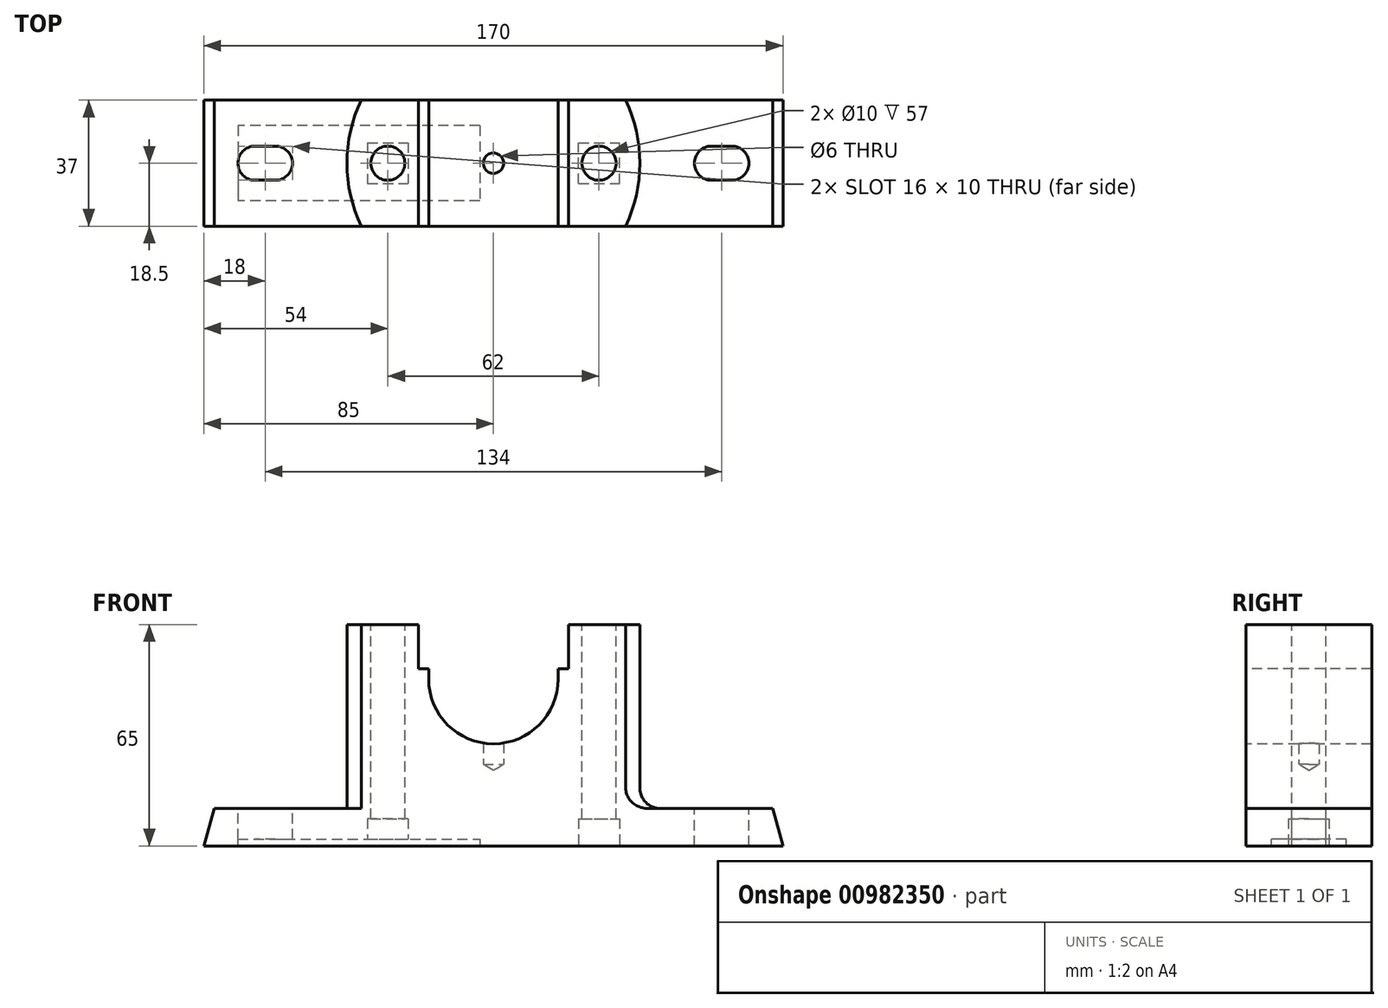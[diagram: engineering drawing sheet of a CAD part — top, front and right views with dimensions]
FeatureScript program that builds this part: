
annotation { "Feature Type Name" : "Feature", "Feature Type Description" : "" }
export const myFeature = defineFeature(function(context is Context, id is Id, definition is map)
    precondition{}
    {
        {
            var Q0;
            Q0=qCreatedBy(makeId("Front.planeOp"),FACE);
            var sketch = newSketch(context, id + "F0", { "sketchPlane" : qUnion([Q0])});
            skLineSegment(sketch, "E0", {"start": v(-85, 0) * mm, "end": v(85, 0) * mm});
            skLineSegment(sketch, "E1", {"start": v(-85, 0) * mm, "end": v(-82, 11) * mm});
            skLineSegment(sketch, "E2", {"start": v(0, 0) * mm, "end": v(0, 40.06) * mm, "construction": true});
            skLineSegment(sketch, "E3.MirrorCS", {"start": v(85, 0) * mm, "end": v(82, 11) * mm});
            skLineSegment(sketch, "E4", {"start": v(-82, 11) * mm, "end": v(82, 11) * mm});
            skSolve(sketch);
        }
        {
            var Q0;
            Q0=qSketchRegion(id+"F0",true);
            extrude(context, id + "F1", {"entities" : qUnion([Q0]), "endBound" : BoundingType.SYMMETRIC, "depth" : 37 * mm, "offsetDistance" : 25 * mm});
        }
        {
            var Q0;
            Q0=makeQuery(id+"F1.opExtrude","SWEPT_FACE",FACE,{"disambiguationData":[OSD([sQuery(id+"F0.wireOp",EDGE,"E4")])]});
            var sketch = newSketch(context, id + "F2", { "sketchPlane" : qUnion([Q0])});
            skArc(sketch, "E5", {"start": v(-38.82, 18.5) * mm, "mid": v(-43, 0) * mm, "end": v(-38.82, -18.5) * mm});
            skLineSegment(sketch, "E6.0", {"start": v(-38.82, 18.5) * mm, "end": v(38.82, 18.5) * mm});
            skLineSegment(sketch, "E6.1", {"start": v(-38.82, -18.5) * mm, "end": v(38.82, -18.5) * mm});
            skPoint(sketch, "E7.orphan", {"position": v(-82, 18.5) * mm});
            skPoint(sketch, "E8.orphan", {"position": v(82, 18.5) * mm});
            skPoint(sketch, "E9.orphan", {"position": v(82, -18.5) * mm});
            skArc(sketch, "E10.trimOffspring", {"start": v(38.82, -18.5) * mm, "mid": v(43, 0) * mm, "end": v(38.82, 18.5) * mm});
            skPoint(sketch, "E11.orphan", {"position": v(-82, -18.5) * mm});
            skSolve(sketch);
        }
        {
            var Q0;
            Q0=makeQuery(id+"F2.imprint","IMPRINT",FACE,{"disambiguationData":[TD([[makeQuery(id+"F2.imprint","IMPRINT",EDGE,{"derivedFrom":sQuery(id+"F2.wireOp",EDGE,"E5")}),1.0]])]});
            extrude(context, id + "F3", {"entities" : qUnion([Q0]), "operationType" : NewBodyOperationType.ADD, "depth" : 54 * mm, "offsetDistance" : 25 * mm});
        }
        {
            var Q0;
            Q0=qCreatedBy(makeId("Front.planeOp"),FACE);
            var sketch = newSketch(context, id + "F4", { "sketchPlane" : qUnion([Q0])});
            skLineSegment(sketch, "E12", {"start": v(-22, 65) * mm, "end": v(-22, 52) * mm});
            skLineSegment(sketch, "E13", {"start": v(-22, 52) * mm, "end": v(-19, 52) * mm});
            skLineSegment(sketch, "E14", {"start": v(-19, 52) * mm, "end": v(-19, 49) * mm});
            skArc(sketch, "E15", {"start": v(-19, 49) * mm, "mid": v(0, 30) * mm, "end": v(19, 49) * mm});
            skLineSegment(sketch, "E16.MirrorCS", {"start": v(22, 52) * mm, "end": v(19, 52) * mm});
            skLineSegment(sketch, "E17.MirrorCS", {"start": v(22, 65) * mm, "end": v(22, 52) * mm});
            skLineSegment(sketch, "E18.MirrorCS", {"start": v(19, 52) * mm, "end": v(19, 49) * mm});
            skLineSegment(sketch, "E19", {"start": v(-22, 65) * mm, "end": v(22, 65) * mm});
            skSolve(sketch);
        }
        {
            var Q0;
            Q0=qSketchRegion(id+"F4",true);
            extrude(context, id + "F5", {"entities" : qUnion([Q0]), "operationType" : NewBodyOperationType.REMOVE, "endBound" : BoundingType.SYMMETRIC, "oppositeDirection" : true, "depth" : 97 * mm, "offsetDistance" : 25 * mm});
        }
        {
            var Q0;
            {var subQ0=sQuery(id+"F2.wireOp",EDGE,"E5");var subQ5=sQuery(id+"F2.wireOp",EDGE,"E6.0");var subQ6=sQuery(id+"F2.wireOp",EDGE,"E6.1");Q0=makeQuery(id+"F5.boolean.opBoolean","SPLIT",FACE,{"disambiguationData":[TD([makeQuery(id+"F3.opExtrude","SWEPT_FACE",FACE,{"disambiguationData":[OSD([subQ0])]})])],"derivedFrom":makeQuery(id+"F3.opExtrude","CAP_FACE",FACE,{"disambiguationData":[OSD([subQ0,subQ5,subQ6,sQuery(id+"F2.wireOp",EDGE,"E10.trimOffspring")])],"isStart":false})});}
            var sketch = newSketch(context, id + "F6", { "sketchPlane" : qUnion([Q0])});
            skLineSegment(sketch, "E20", {"start": v(0, 0) * mm, "end": v(0, 69.04) * mm, "construction": true});
            skCircle(sketch, "E21", {"center": v(-31, 0) * mm, "radius": 5 * mm});
            skCircle(sketch, "E22.MirrorC", {"center": v(31, 0) * mm, "radius": 5 * mm});
            skSolve(sketch);
        }
        {
            var Q0;
            Q0=qSketchRegion(id+"F6",true);
            extrude(context, id + "F7", {"entities" : qUnion([Q0]), "operationType" : NewBodyOperationType.REMOVE, "endBound" : BoundingType.THROUGH_ALL, "oppositeDirection" : true, "depth" : 25 * mm, "offsetDistance" : 25 * mm});
        }
        {
            var Q0;
            Q0=makeQuery(id+"F1.opExtrude","SWEPT_FACE",FACE,{"disambiguationData":[OSD([sQuery(id+"F0.wireOp",EDGE,"E0")])]});
            var sketch = newSketch(context, id + "F8", { "sketchPlane" : qUnion([Q0])});
            skLineSegment(sketch, "E23.bottom", {"start": v(-25, 6) * mm, "end": v(-37, 6) * mm});
            skLineSegment(sketch, "E23.top", {"start": v(-25, -6) * mm, "end": v(-37, -6) * mm});
            skLineSegment(sketch, "E23.left", {"start": v(-25, 6) * mm, "end": v(-25, -6) * mm});
            skLineSegment(sketch, "E23.right", {"start": v(-37, 6) * mm, "end": v(-37, -6) * mm});
            skPoint(sketch, "E23.middle", {"position": v(-31, 0) * mm});
            skLineSegment(sketch, "E24.MirrorCS", {"start": v(25, 6) * mm, "end": v(25, -6) * mm});
            skLineSegment(sketch, "E25.MirrorCS", {"start": v(25, 6) * mm, "end": v(37, 6) * mm});
            skLineSegment(sketch, "E26.MirrorCS", {"start": v(37, 6) * mm, "end": v(37, -6) * mm});
            skLineSegment(sketch, "E27.MirrorCS", {"start": v(25, -6) * mm, "end": v(37, -6) * mm});
            skSolve(sketch);
        }
        {
            var Q0;
            Q0=qSketchRegion(id+"F8",true);
            extrude(context, id + "F9", {"entities" : qUnion([Q0]), "operationType" : NewBodyOperationType.REMOVE, "oppositeDirection" : true, "depth" : 8 * mm, "offsetDistance" : 25 * mm});
        }
        {
            var Q0;
            Q0=qCreatedBy(makeId("Front.planeOp"),FACE);
            var sketch = newSketch(context, id + "F10", { "sketchPlane" : qUnion([Q0])});
            skLineSegment(sketch, "E28", {"start": v(-75, 0) * mm, "end": v(-75, 2) * mm});
            skLineSegment(sketch, "E29", {"start": v(-75, 2) * mm, "end": v(-4, 2) * mm});
            skLineSegment(sketch, "E30", {"start": v(-4, 2) * mm, "end": v(-4, 0) * mm});
            skLineSegment(sketch, "E31", {"start": v(-4, 0) * mm, "end": v(-75, 0) * mm});
            skLineSegment(sketch, "E32", {"start": v(0, 0) * mm, "end": v(0, 73.2) * mm, "construction": true});
            skLineSegment(sketch, "E33", {"start": v(0, 73.2) * mm, "end": v(-67, 73.2) * mm, "construction": true});
            skLineSegment(sketch, "E34", {"start": v(-67, 73.2) * mm, "end": v(-67, 9.2) * mm, "construction": true});
            skLineSegment(sketch, "E35", {"start": v(-67, 9.2) * mm, "end": v(-75, 9.2) * mm, "construction": true});
            skLineSegment(sketch, "E36", {"start": v(-75, 9.2) * mm, "end": v(-59, 9.2) * mm, "construction": true});
            skSolve(sketch);
        }
        {
            var Q0;
            Q0=qSketchRegion(id+"F10",true);
            extrude(context, id + "F11", {"entities" : qUnion([Q0]), "operationType" : NewBodyOperationType.REMOVE, "endBound" : BoundingType.SYMMETRIC, "oppositeDirection" : true, "depth" : 22 * mm, "offsetDistance" : 25 * mm});
        }
        {
            var Q0;
            {var subQ0=sQuery(id+"F0.wireOp",EDGE,"E4");var subQ2=sQuery(id+"F0.wireOp",EDGE,"E1");Q0=makeQuery(id+"F3.boolean.opBoolean","SPLIT",FACE,{"disambiguationData":[TD([makeQuery(id+"F1.opExtrude","SWEPT_FACE",FACE,{"disambiguationData":[OSD([subQ2])]})])],"derivedFrom":makeQuery(id+"F1.opExtrude","SWEPT_FACE",FACE,{"disambiguationData":[OSD([subQ0])]})});}
            var sketch = newSketch(context, id + "F12", { "sketchPlane" : qUnion([Q0])});
            skLineSegment(sketch, "E37", {"start": v(-70, 0) * mm, "end": v(-64, 0) * mm});
            skArc(sketch, "E38.0.startCap", {"start": v(-70, -5) * mm, "mid": v(-75, 0) * mm, "end": v(-70, 5) * mm});
            skArc(sketch, "E38.0.endCap", {"start": v(-64, 5) * mm, "mid": v(-59, 0) * mm, "end": v(-64, -5) * mm});
            skLineSegment(sketch, "E38.0.left", {"start": v(-70, 5) * mm, "end": v(-64, 5) * mm});
            skLineSegment(sketch, "E38.0.right", {"start": v(-70, -5) * mm, "end": v(-64, -5) * mm});
            skLineSegment(sketch, "E39", {"start": v(-67, 0) * mm, "end": v(-67, 10.76) * mm, "construction": true});
            skLineSegment(sketch, "E40", {"start": v(-59, 0) * mm, "end": v(-59, 0) * mm});
            skLineSegment(sketch, "E41.MirrorCS", {"start": v(70, 0) * mm, "end": v(64, 0) * mm});
            skLineSegment(sketch, "E42.MirrorCS", {"start": v(70, 5) * mm, "end": v(64, 5) * mm});
            skLineSegment(sketch, "E43.MirrorCS", {"start": v(70, -5) * mm, "end": v(64, -5) * mm});
            skArc(sketch, "E44.MirrorCS", {"start": v(64, 5) * mm, "mid": v(59, 0) * mm, "end": v(64, -5) * mm});
            skLineSegment(sketch, "E45.MirrorCS", {"start": v(59, 0) * mm, "end": v(59, 0) * mm});
            skArc(sketch, "E46.MirrorCS", {"start": v(70, -5) * mm, "mid": v(75, 0) * mm, "end": v(70, 5) * mm});
            skSolve(sketch);
        }
        {
            var Q0;
            Q0=qSketchRegion(id+"F12",true);
            extrude(context, id + "F13", {"entities" : qUnion([Q0]), "operationType" : NewBodyOperationType.REMOVE, "endBound" : BoundingType.THROUGH_ALL, "oppositeDirection" : true, "depth" : 25 * mm, "offsetDistance" : 25 * mm});
        }
        {
            var Q0;
            Q0=qCreatedBy(makeId("Front.planeOp"),FACE);
            var sketch = newSketch(context, id + "F14", { "sketchPlane" : qUnion([Q0])});
            skLineSegment(sketch, "E47", {"start": v(0, 31.8) * mm, "end": v(0, 22.2) * mm});
            skLineSegment(sketch, "E48", {"start": v(0, 22.2) * mm, "end": v(3, 24) * mm});
            skLineSegment(sketch, "E49", {"start": v(3, 24) * mm, "end": v(3, 31.8) * mm});
            skLineSegment(sketch, "E50", {"start": v(3, 31.8) * mm, "end": v(0, 31.8) * mm});
            skSolve(sketch);
        }
        {
            var Q0;
            Q0=qSketchRegion(id+"F14",true);
            var Q1;
            Q1=sQuery(id+"F14.wireOp",EDGE,"E47");
            revolve(context, id + "F15", {"operationType" : NewBodyOperationType.REMOVE, "surfaceOperationType" : NewSurfaceOperationType.NEW, "entities" : qUnion([Q0]), "axis" : qUnion([Q1]), "revolveType" : RevolveType.FULL, "oppositeDirection" : true});
        }
        {
            var Q0;
            Q0=makeQuery(id+"F14.imprint","IMPRINT",FACE,{"disambiguationData":[TD([[makeQuery(id+"F14.imprint","IMPRINT",EDGE,{"derivedFrom":sQuery(id+"F14.wireOp",EDGE,"E47")}),1.0]])]});
            var Q1;
            Q1=sQuery(id+"F14.wireOp",EDGE,"E47");
            revolve(context, id + "F16", {"operationType" : NewBodyOperationType.REMOVE, "surfaceOperationType" : NewSurfaceOperationType.NEW, "entities" : qUnion([Q0]), "axis" : qUnion([Q1]), "revolveType" : RevolveType.FULL, "oppositeDirection" : true});
        }
        {
            var Q0;
            Q0=makeQuery(id+"F3.opExtrude","CAP_EDGE",EDGE,{"disambiguationData":[OSD([sQuery(id+"F2.wireOp",EDGE,"E10.trimOffspring")])],"isStart":true});
            var Q1;
            Q1=makeQuery(id+"F3.opExtrude","CAP_EDGE",EDGE,{"disambiguationData":[OSD([sQuery(id+"F2.wireOp",EDGE,"E5")])],"isStart":true});
            fillet(context, id + "F17", {"entities" : qUnion([Q0, Q1]), "radius" : 6 * mm, "tangentPropagation" : true, "allowEdgeOverflow" : false});
        }
    });
